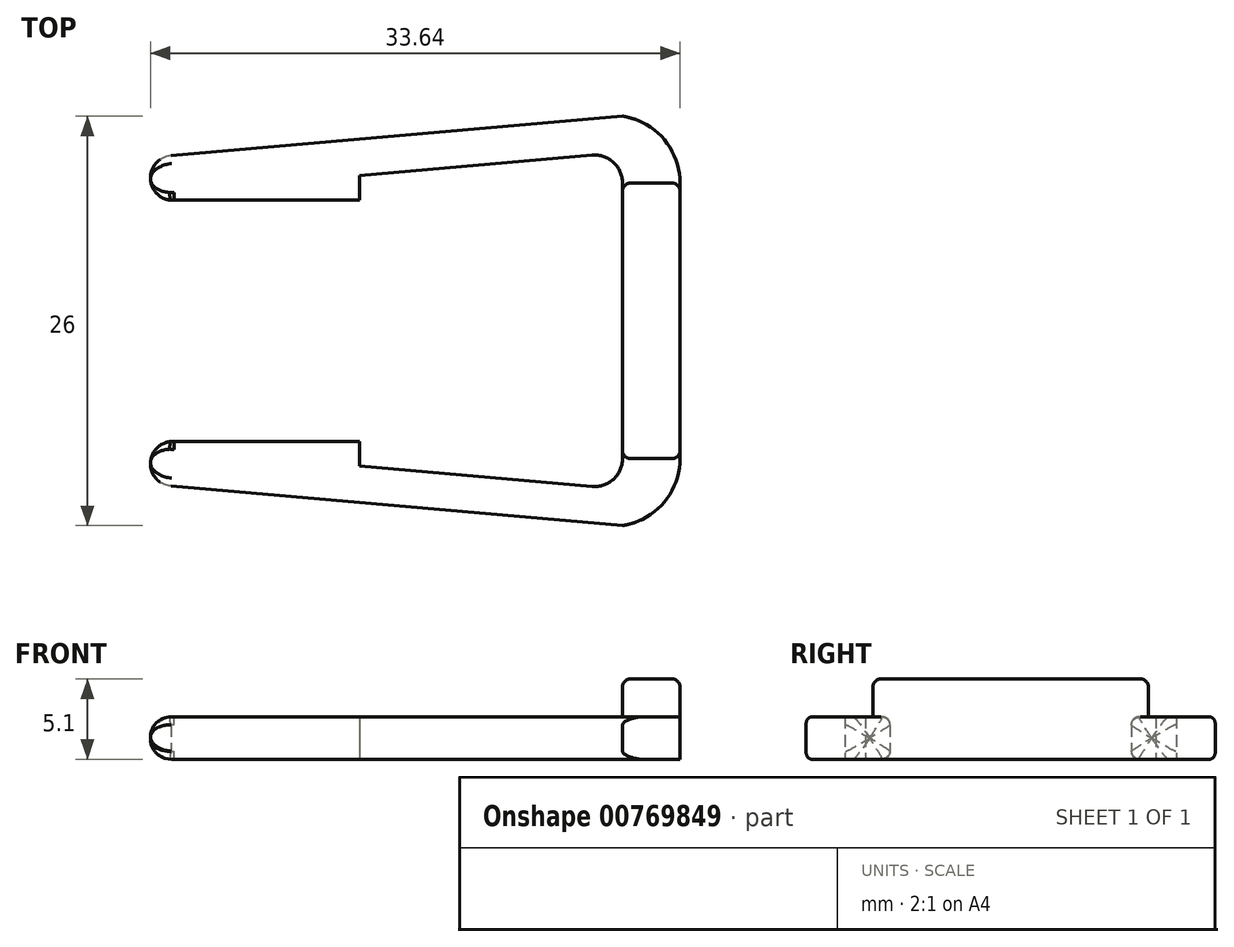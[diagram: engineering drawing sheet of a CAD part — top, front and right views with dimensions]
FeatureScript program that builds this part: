
annotation { "Feature Type Name" : "Feature", "Feature Type Description" : "" }
export const myFeature = defineFeature(function(context is Context, id is Id, definition is map)
    precondition{}
    {
        {
            var Q0;
            Q0=qCreatedBy(makeId("Top.planeOp"),FACE);
            var sketch = newSketch(context, id + "F0", { "sketchPlane" : qUnion([Q0])});
            skLineSegment(sketch, "E0", {"start": v(1.77, 0) * mm, "end": v(1.77, 12) * mm});
            skLineSegment(sketch, "E1", {"start": v(1.77, 12) * mm, "end": v(-28.7, 9.34) * mm});
            skLineSegment(sketch, "E2", {"start": v(0, 13) * mm, "end": v(-28.7, 10.49) * mm});
            skLineSegment(sketch, "E3", {"start": v(0, 0) * mm, "end": v(3.65, 0) * mm});
            skLineSegment(sketch, "E4", {"start": v(3.65, 0) * mm, "end": v(3.65, 8.75) * mm});
            skArc(sketch, "E5", {"start": v(3.65, 8.75) * mm, "mid": v(2.61, 11.55) * mm, "end": v(0, 13) * mm});
            skLineSegment(sketch, "E6", {"start": v(0, 0) * mm, "end": v(0, 8.75) * mm});
            skLineSegment(sketch, "E7", {"start": v(-16.7, 9.23) * mm, "end": v(-1.93, 10.52) * mm});
            skArc(sketch, "E8", {"start": v(0, 8.75) * mm, "mid": v(-0.58, 10.06) * mm, "end": v(-1.93, 10.52) * mm});
            skLineSegment(sketch, "E9", {"start": v(-16.7, 9.23) * mm, "end": v(-16.7, 7.66) * mm});
            skLineSegment(sketch, "E10", {"start": v(-16.7, 7.66) * mm, "end": v(-28.7, 7.66) * mm});
            skLineSegment(sketch, "E11", {"start": v(-28.7, 10.49) * mm, "end": v(-28.7, 7.66) * mm});
            skArc(sketch, "E12", {"start": v(-28.7, 10.49) * mm, "mid": v(-29.99, 9.08) * mm, "end": v(-28.7, 7.66) * mm});
            skLineSegment(sketch, "E13", {"start": v(0, 8.75) * mm, "end": v(3.65, 8.75) * mm});
            skSolve(sketch);
        }
        {
            var Q0;
            Q0=qSketchRegion(id+"F0",true);
            extrude(context, id + "F1", {"entities" : qUnion([Q0]), "depth" : 2.7 * mm, "offsetDistance" : 25 * mm});
        }
        {
            var Q0;
            Q0=makeQuery(id+"F1.opExtrude","CAP_FACE",FACE,{"disambiguationData":[OSD([sQuery(id+"F0.wireOp",EDGE,"E2"),sQuery(id+"F0.wireOp",EDGE,"E3"),sQuery(id+"F0.wireOp",EDGE,"E4"),sQuery(id+"F0.wireOp",EDGE,"E5"),sQuery(id+"F0.wireOp",EDGE,"E6"),sQuery(id+"F0.wireOp",EDGE,"E7"),sQuery(id+"F0.wireOp",EDGE,"E8"),sQuery(id+"F0.wireOp",EDGE,"E9"),sQuery(id+"F0.wireOp",EDGE,"E10"),sQuery(id+"F0.wireOp",EDGE,"E12")])],"isStart":false});
            var sketch = newSketch(context, id + "F2", { "sketchPlane" : qUnion([Q0])});
            skPoint(sketch, "E14.0", {"position": v(0, 8.75) * mm});
            skPoint(sketch, "E15.0", {"position": v(3.65, 8.75) * mm});
            skLineSegment(sketch, "E16.bottom", {"start": v(0, 8.75) * mm, "end": v(3.65, 8.75) * mm});
            skLineSegment(sketch, "E16.top", {"start": v(0, 0) * mm, "end": v(3.65, 0) * mm});
            skLineSegment(sketch, "E16.left", {"start": v(0, 8.75) * mm, "end": v(0, 0) * mm});
            skLineSegment(sketch, "E16.right", {"start": v(3.65, 8.75) * mm, "end": v(3.65, 0) * mm});
            skSolve(sketch);
        }
        {
            var Q0;
            Q0=qSketchRegion(id+"F2",true);
            extrude(context, id + "F3", {"entities" : qUnion([Q0]), "operationType" : NewBodyOperationType.ADD, "depth" : 2.4 * mm, "offsetDistance" : 25 * mm});
        }
        {
            var Q0;
            Q0=makeQuery(id+"F1.opExtrude","SWEPT_FACE",FACE,{"disambiguationData":[OSD([sQuery(id+"F0.wireOp",EDGE,"E2")])]});
            var sketch = newSketch(context, id + "F4", { "sketchPlane" : qUnion([Q0])});
            skLineSegment(sketch, "E17", {"start": v(29.09, 2.7) * mm, "end": v(29.09, 0) * mm});
            skLineSegment(sketch, "E18.0", {"start": v(27.67, 2.7) * mm, "end": v(27.67, 0) * mm});
            skEllipse(sketch, "E19", {"center": v(27.67, 1.35) * mm, "majorRadius": 1.35 * mm, "minorRadius": 1.42 * mm, "majorAxis": v(0, 1)});
            skLineSegment(sketch, "E20", {"start": v(27.67, 2.7) * mm, "end": v(29.09, 2.7) * mm});
            skLineSegment(sketch, "E21.0", {"start": v(27.67, 0) * mm, "end": v(29.09, 0) * mm});
            skSolve(sketch);
        }
        {
            var Q0;
            {var subQ0=sQuery(id+"F4.wireOp",EDGE,"E20");Q0=makeQuery(id+"F4.imprint","IMPRINT",FACE,{"disambiguationData":[TD([[makeQuery(id+"F4.imprint","IMPRINT",EDGE,{"derivedFrom":subQ0}),-1.0]])]});}
            var Q1;
            {var subQ0=sQuery(id+"F4.wireOp",EDGE,"E21.0");Q1=makeQuery(id+"F4.imprint","IMPRINT",FACE,{"disambiguationData":[TD([[makeQuery(id+"F4.imprint","IMPRINT",EDGE,{"derivedFrom":subQ0}),1.0]])]});}
            extrude(context, id + "F5", {"entities" : qUnion([Q0, Q1]), "operationType" : NewBodyOperationType.REMOVE, "endBound" : BoundingType.THROUGH_ALL, "oppositeDirection" : true, "depth" : 25 * mm, "offsetDistance" : 25 * mm});
        }
        {
            var Q0;
            Q0=makeQuery(id+"F3.opExtrude","SWEPT_EDGE",EDGE,{"disambiguationData":[OSD([sQuery(id+"F0.wireOp",EDGE,"E8"),sQuery(id+"F2.wireOp",EDGE,"E16.bottom"),sQuery(id+"F2.wireOp",EDGE,"E16.left")])]});
            var Q1;
            Q1=makeQuery(id+"F3.opExtrude","CAP_EDGE",EDGE,{"disambiguationData":[OSD([sQuery(id+"F2.wireOp",EDGE,"E16.bottom")])],"isStart":false});
            var Q2;
            Q2=makeQuery(id+"F3.opExtrude","SWEPT_EDGE",EDGE,{"disambiguationData":[OSD([sQuery(id+"F0.wireOp",EDGE,"E5"),sQuery(id+"F2.wireOp",EDGE,"E16.bottom"),sQuery(id+"F2.wireOp",EDGE,"E16.right")])]});
            var Q3;
            Q3=makeQuery(id+"F3.opExtrude","CAP_EDGE",EDGE,{"disambiguationData":[OSD([sQuery(id+"F2.wireOp",EDGE,"E16.left")])],"isStart":false});
            var Q4;
            Q4=makeQuery(id+"F3.opExtrude","CAP_EDGE",EDGE,{"disambiguationData":[OSD([sQuery(id+"F2.wireOp",EDGE,"E16.right")])],"isStart":false});
            var Q5;
            Q5=makeQuery(id+"F1.opExtrude","CAP_EDGE",EDGE,{"disambiguationData":[OSD([sQuery(id+"F0.wireOp",EDGE,"E2")])],"isStart":false});
            var Q6;
            Q6=makeQuery(id+"F1.opExtrude","CAP_EDGE",EDGE,{"disambiguationData":[OSD([sQuery(id+"F0.wireOp",EDGE,"E2")])],"isStart":true});
            var Q7;
            Q7=makeQuery(id+"F1.opExtrude","CAP_EDGE",EDGE,{"disambiguationData":[OSD([sQuery(id+"F0.wireOp",EDGE,"E10")])],"isStart":false});
            var Q8;
            Q8=makeQuery(id+"F1.opExtrude","CAP_EDGE",EDGE,{"disambiguationData":[OSD([sQuery(id+"F0.wireOp",EDGE,"E10")])],"isStart":true});
            fillet(context, id + "F6", {"entities" : qUnion([Q0, Q1, Q2, Q3, Q4, Q5, Q6, Q7, Q8]), "radius" : .5 * mm, "tangentPropagation" : true, "allowEdgeOverflow" : false});
        }
        {
            var Q0;
            Q0=makeQuery(id+"F1.opExtrude","SWEPT_BODY",BODY,{"disambiguationData":[OSD([sQuery(id+"F0.wireOp",EDGE,"E2"),sQuery(id+"F0.wireOp",EDGE,"E3"),sQuery(id+"F0.wireOp",EDGE,"E4"),sQuery(id+"F0.wireOp",EDGE,"E5"),sQuery(id+"F0.wireOp",EDGE,"E6"),sQuery(id+"F0.wireOp",EDGE,"E7"),sQuery(id+"F0.wireOp",EDGE,"E8"),sQuery(id+"F0.wireOp",EDGE,"E9"),sQuery(id+"F0.wireOp",EDGE,"E10"),sQuery(id+"F0.wireOp",EDGE,"E12")])]});
            var Q1;
            Q1=makeQuery(id+"F3.boolean.opBoolean","MERGE",FACE,{"derivedFrom":[makeQuery(id+"F1.opExtrude","SWEPT_FACE",FACE,{"disambiguationData":[OSD([sQuery(id+"F0.wireOp",EDGE,"E3")])]}),makeQuery(id+"F3.opExtrude","SWEPT_FACE",FACE,{"disambiguationData":[OSD([sQuery(id+"F2.wireOp",EDGE,"E16.top")])]})]});
            mirror(context, id + "F7", {"operationType" : NewBodyOperationType.ADD, "entities" : qUnion([Q0]), "mirrorPlane" : qUnion([Q1])});
        }
    });
